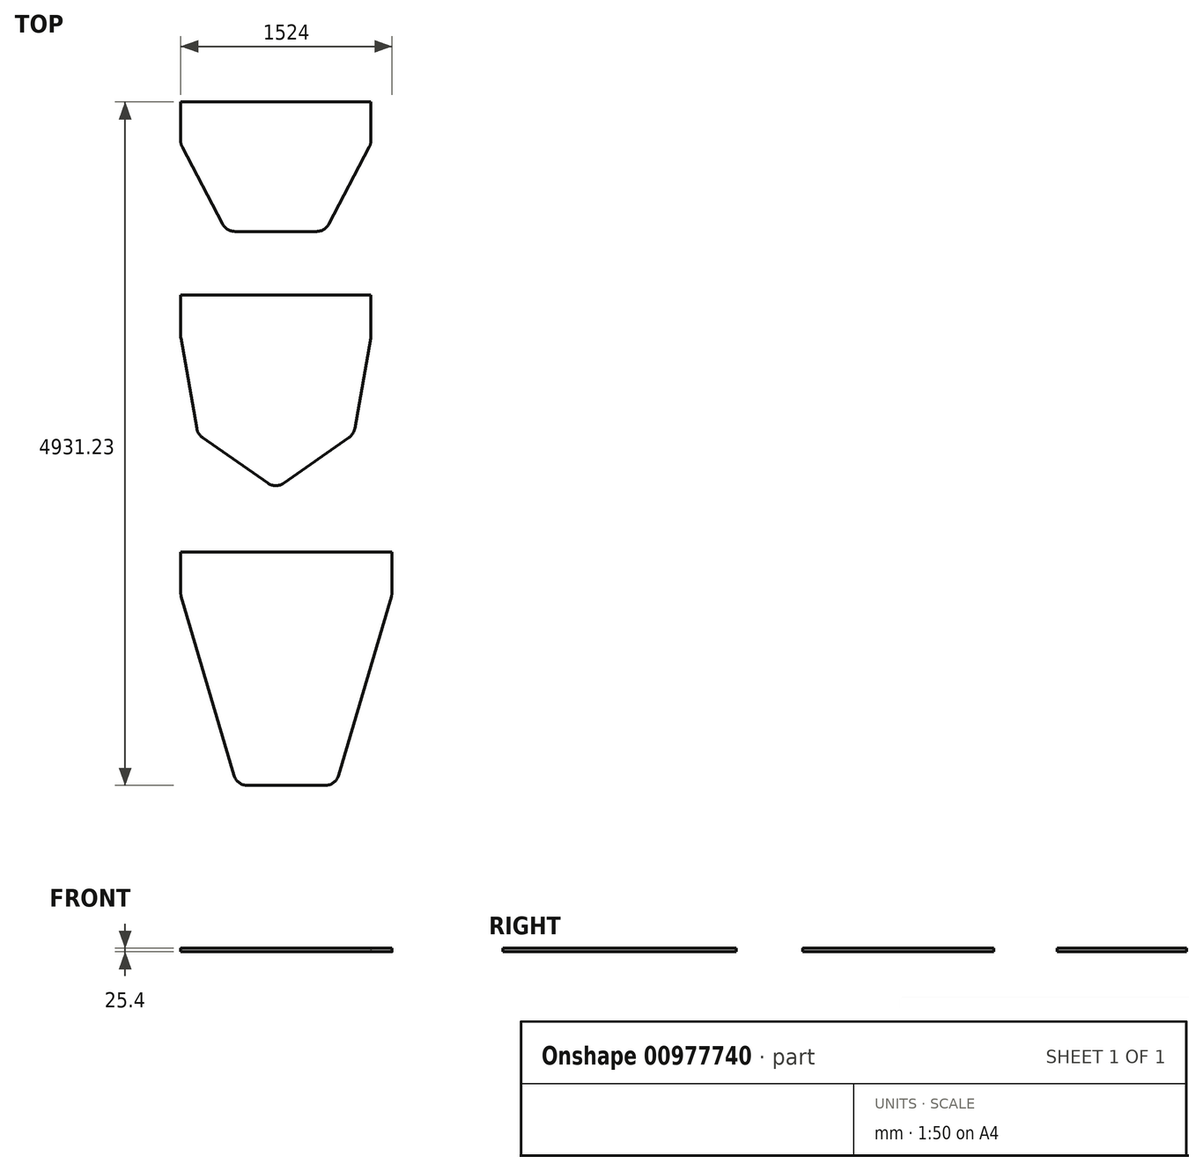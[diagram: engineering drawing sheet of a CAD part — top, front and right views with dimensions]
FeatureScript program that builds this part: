
annotation { "Feature Type Name" : "Feature", "Feature Type Description" : "" }
export const myFeature = defineFeature(function(context is Context, id is Id, definition is map)
    precondition{}
    {
        {
            var Q0;
            Q0=qCreatedBy(makeId("Top.planeOp"),FACE);
            var sketch = newSketch(context, id + "F0", { "sketchPlane" : qUnion([Q0])});
            skLineSegment(sketch, "E0.bottom", {"start": v(0, 0) * mm, "end": v(1371.6, 0) * mm});
            skLineSegment(sketch, "E0.top", {"start": v(0, -304.8) * mm, "end": v(1371.6, -304.8) * mm, "construction": true});
            skLineSegment(sketch, "E0.left", {"start": v(0, 0) * mm, "end": v(0, -279.78) * mm});
            skLineSegment(sketch, "E0.right", {"start": v(1371.6, 0) * mm, "end": v(1371.6, -279.78) * mm});
            skLineSegment(sketch, "E1", {"start": v(11.61, -326.96) * mm, "end": v(301.67, -880.27) * mm});
            skLineSegment(sketch, "E2", {"start": v(391.65, -934.7) * mm, "end": v(979.95, -934.7) * mm});
            skLineSegment(sketch, "E3", {"start": v(1069.93, -880.27) * mm, "end": v(1359.99, -326.96) * mm});
            skLineSegment(sketch, "E4.bottom", {"start": v(0, -1391.9) * mm, "end": v(1371.6, -1391.9) * mm});
            skLineSegment(sketch, "E4.top", {"start": v(0, -1696.7) * mm, "end": v(1371.6, -1696.7) * mm, "construction": true});
            skLineSegment(sketch, "E4.left", {"start": v(0, -1391.9) * mm, "end": v(0, -1687.81) * mm});
            skLineSegment(sketch, "E4.right", {"start": v(1371.6, -1391.9) * mm, "end": v(1371.6, -1687.81) * mm});
            skLineSegment(sketch, "E5", {"start": v(1255.4, -2355.65) * mm, "end": v(1370.06, -1705.45) * mm});
            skLineSegment(sketch, "E6", {"start": v(61.75, -2046.9) * mm, "end": v(685.8, -1391.9) * mm, "construction": true});
            skLineSegment(sketch, "E7", {"start": v(0, -304.8) * mm, "end": v(0, -1391.9) * mm, "construction": true});
            skLineSegment(sketch, "E8", {"start": v(1.54, -1705.45) * mm, "end": v(116.2, -2355.65) * mm});
            skLineSegment(sketch, "E9", {"start": v(685.8, 0) * mm, "end": v(685.8, -152.4) * mm, "construction": true});
            skLineSegment(sketch, "E10", {"start": v(685.8, -152.4) * mm, "end": v(165.1, -619.75) * mm, "construction": true});
            skLineSegment(sketch, "E11", {"start": v(685.8, -152.4) * mm, "end": v(393.04, -304.8) * mm, "construction": true});
            skLineSegment(sketch, "E12", {"start": v(685.8, -152.4) * mm, "end": v(978.56, -304.8) * mm, "construction": true});
            skLineSegment(sketch, "E13", {"start": v(685.8, -1391.9) * mm, "end": v(685.8, -1544.3) * mm, "construction": true});
            skLineSegment(sketch, "E14", {"start": v(685.8, -1544.3) * mm, "end": v(393.04, -1696.7) * mm, "construction": true});
            skLineSegment(sketch, "E15", {"start": v(685.8, -1544.3) * mm, "end": v(978.56, -1696.7) * mm, "construction": true});
            skLineSegment(sketch, "E16", {"start": v(157.97, -2421.23) * mm, "end": v(627.52, -2750.02) * mm});
            skLineSegment(sketch, "E17", {"start": v(744.08, -2750.02) * mm, "end": v(1213.63, -2421.23) * mm});
            skLineSegment(sketch, "E18", {"start": v(685.8, -1544.3) * mm, "end": v(685.8, -2790.82) * mm, "construction": true});
            skPoint(sketch, "E19.0.visualSharp", {"position": v(0, -1696.7) * mm});
            skArc(sketch, "E19.0.filletArc", {"start": v(0, -1687.81) * mm, "mid": v(0.39, -1696.67) * mm, "end": v(1.54, -1705.45) * mm});
            skPoint(sketch, "E20.0.visualSharp", {"position": v(123.5, -2397.1) * mm});
            skArc(sketch, "E20.0.filletArc", {"start": v(116.2, -2355.65) * mm, "mid": v(130.56, -2392.6) * mm, "end": v(157.97, -2421.23) * mm});
            skPoint(sketch, "E21.0.visualSharp", {"position": v(685.8, -2790.82) * mm});
            skArc(sketch, "E21.0.filletArc", {"start": v(627.52, -2750.02) * mm, "mid": v(685.8, -2768.4) * mm, "end": v(744.08, -2750.02) * mm});
            skPoint(sketch, "E21.1.visualSharp", {"position": v(1248.1, -2397.1) * mm});
            skArc(sketch, "E21.1.filletArc", {"start": v(1213.63, -2421.23) * mm, "mid": v(1241.04, -2392.6) * mm, "end": v(1255.4, -2355.65) * mm});
            skPoint(sketch, "E21.2.visualSharp", {"position": v(1371.6, -1696.7) * mm});
            skArc(sketch, "E21.2.filletArc", {"start": v(1370.06, -1705.45) * mm, "mid": v(1371.21, -1696.67) * mm, "end": v(1371.6, -1687.81) * mm});
            skLineSegment(sketch, "E22", {"start": v(216.25, -2338) * mm, "end": v(1155.35, -2338) * mm, "construction": true});
            skPoint(sketch, "E23.0.visualSharp", {"position": v(0, -304.8) * mm});
            skArc(sketch, "E23.0.filletArc", {"start": v(0, -279.78) * mm, "mid": v(2.95, -304.07) * mm, "end": v(11.61, -326.96) * mm});
            skPoint(sketch, "E23.1.visualSharp", {"position": v(330.2, -934.7) * mm});
            skArc(sketch, "E23.1.filletArc", {"start": v(301.67, -880.27) * mm, "mid": v(339.07, -920.03) * mm, "end": v(391.65, -934.7) * mm});
            skPoint(sketch, "E23.2.visualSharp", {"position": v(1041.4, -934.7) * mm});
            skArc(sketch, "E23.2.filletArc", {"start": v(979.95, -934.7) * mm, "mid": v(1032.53, -920.03) * mm, "end": v(1069.93, -880.27) * mm});
            skPoint(sketch, "E23.3.visualSharp", {"position": v(1371.6, -304.8) * mm});
            skArc(sketch, "E23.3.filletArc", {"start": v(1359.99, -326.96) * mm, "mid": v(1368.65, -304.07) * mm, "end": v(1371.6, -279.78) * mm});
            skLineSegment(sketch, "E24", {"start": v(391.65, -833.1) * mm, "end": v(979.95, -833.1) * mm, "construction": true});
            skLineSegment(sketch, "E25", {"start": v(101.6, -279.78) * mm, "end": v(1270, -279.78) * mm, "construction": true});
            skLineSegment(sketch, "E26.bottom", {"start": v(0, -3248.02) * mm, "end": v(1524, -3248.02) * mm});
            skLineSegment(sketch, "E26.top", {"start": v(0, -3552.82) * mm, "end": v(1524, -3552.82) * mm, "construction": true});
            skLineSegment(sketch, "E26.left", {"start": v(0, -3248.02) * mm, "end": v(0, -3538.16) * mm});
            skLineSegment(sketch, "E26.right", {"start": v(1524, -3248.02) * mm, "end": v(1524, -3538.16) * mm});
            skLineSegment(sketch, "E27", {"start": v(1139.08, -4858.36) * mm, "end": v(1519.85, -3566.89) * mm});
            skLineSegment(sketch, "E28", {"start": v(205.27, -4249.06) * mm, "end": v(762, -3248.02) * mm, "construction": true});
            skLineSegment(sketch, "E29", {"start": v(0, -1687.81) * mm, "end": v(0, -3248.02) * mm, "construction": true});
            skLineSegment(sketch, "E30", {"start": v(4.15, -3566.89) * mm, "end": v(384.92, -4858.36) * mm});
            skLineSegment(sketch, "E31", {"start": v(762, -3248.02) * mm, "end": v(762, -3400.42) * mm, "construction": true});
            skLineSegment(sketch, "E32", {"start": v(762, -3400.42) * mm, "end": v(469.24, -3552.82) * mm, "construction": true});
            skLineSegment(sketch, "E33", {"start": v(762, -3400.42) * mm, "end": v(1054.76, -3552.82) * mm, "construction": true});
            skLineSegment(sketch, "E34", {"start": v(762, -3400.42) * mm, "end": v(762, -4931.23) * mm, "construction": true});
            skPoint(sketch, "E35.0.visualSharp", {"position": v(0, -3552.82) * mm});
            skArc(sketch, "E35.0.filletArc", {"start": v(0, -3538.16) * mm, "mid": v(1.04, -3552.67) * mm, "end": v(4.15, -3566.89) * mm});
            skPoint(sketch, "E36.2.visualSharp", {"position": v(1524, -3552.82) * mm});
            skArc(sketch, "E36.2.filletArc", {"start": v(1519.85, -3566.89) * mm, "mid": v(1522.96, -3552.67) * mm, "end": v(1524, -3538.16) * mm});
            skLineSegment(sketch, "E37", {"start": v(482.37, -4829.63) * mm, "end": v(1041.63, -4829.63) * mm, "construction": true});
            skLineSegment(sketch, "E38", {"start": v(482.37, -4931.23) * mm, "end": v(1041.63, -4931.23) * mm});
            skLineSegment(sketch, "E39", {"start": v(101.6, -3538.16) * mm, "end": v(1422.4, -3538.16) * mm, "construction": true});
            skPoint(sketch, "E40.0.visualSharp", {"position": v(406.4, -4931.23) * mm});
            skArc(sketch, "E40.0.filletArc", {"start": v(384.92, -4858.36) * mm, "mid": v(421.53, -4911) * mm, "end": v(482.37, -4931.23) * mm});
            skPoint(sketch, "E40.1.visualSharp", {"position": v(1117.6, -4931.23) * mm});
            skArc(sketch, "E40.1.filletArc", {"start": v(1041.63, -4931.23) * mm, "mid": v(1102.47, -4911) * mm, "end": v(1139.08, -4858.36) * mm});
            skSolve(sketch);
        }
        {
            var Q0;
            Q0 = qSketchRegion(id + "F0", true);
            extrude(context, id + "F1", {"entities" : qUnion([Q0]), "domain" : OperationDomain.MODEL, "flatOperationType" : FlatOperationType.REMOVE, "depth" : 25.4 * mm, "offsetDistance" : 25.4 * mm});
        }
    });
